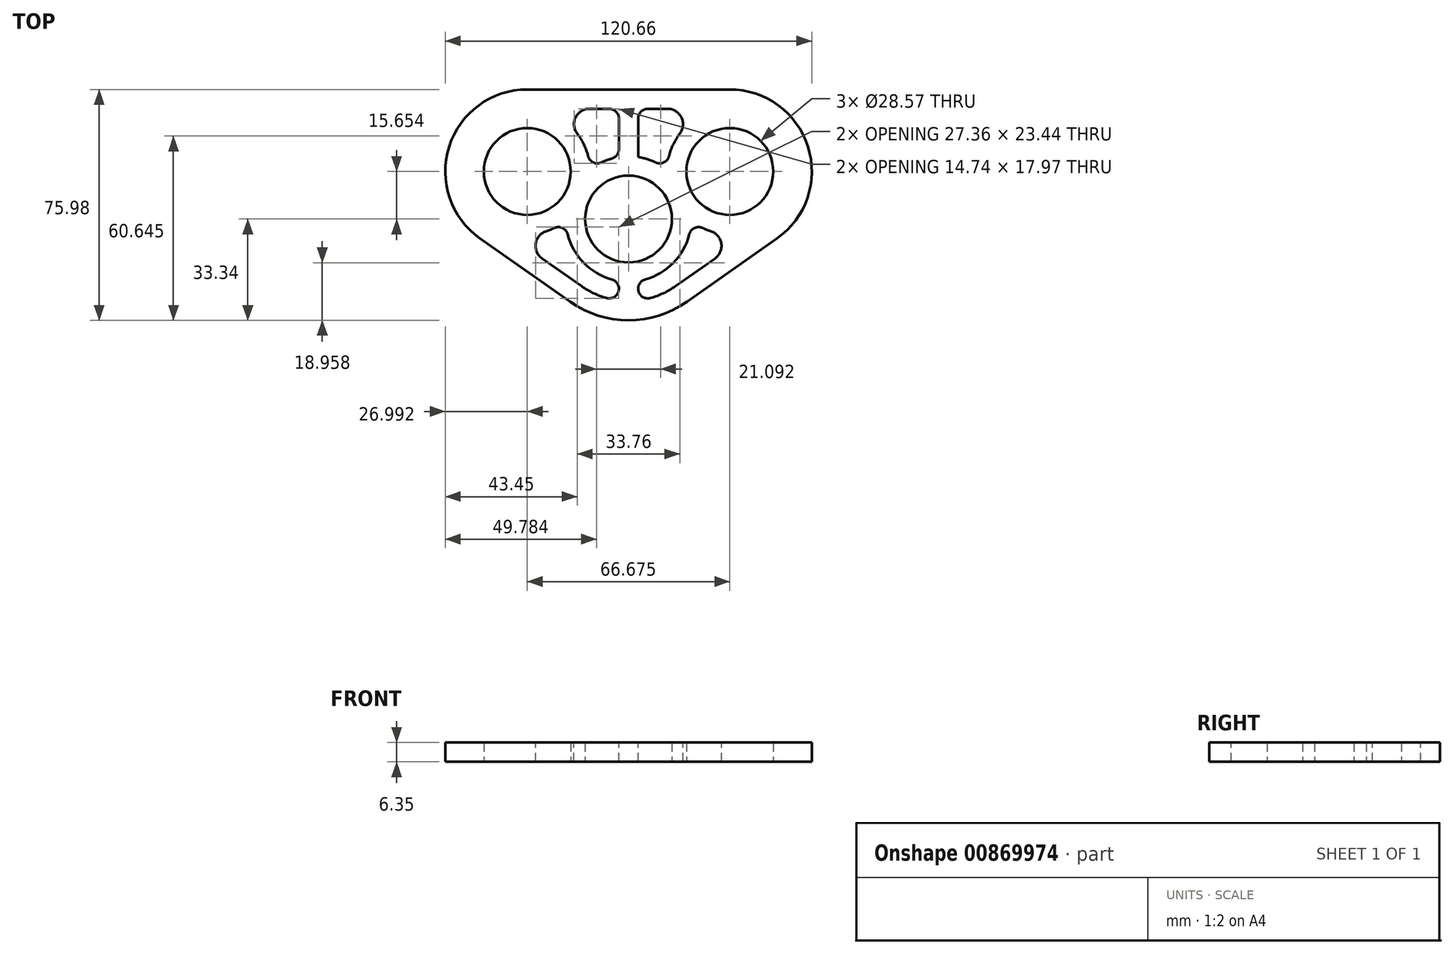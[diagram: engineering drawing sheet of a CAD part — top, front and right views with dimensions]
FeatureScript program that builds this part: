
annotation { "Feature Type Name" : "Feature", "Feature Type Description" : "" }
export const myFeature = defineFeature(function(context is Context, id is Id, definition is map)
    precondition{}
    {
        {
            var Q0;
            Q0=qCreatedBy(makeId("Top.planeOp"),FACE);
            var sketch = newSketch(context, id + "F0", { "sketchPlane" : qUnion([Q0])});
            skCircle(sketch, "E0", {"center": v(0, 0) * mm, "radius": 27.94 * mm, "construction": true});
            skCircle(sketch, "E1.0", {"center": v(0, 0) * mm, "radius": 30.48 * mm, "construction": true});
            skCircle(sketch, "E2", {"center": v(-33.34, 15.65) * mm, "radius": 8.9 * mm, "construction": true});
            skCircle(sketch, "E3.0", {"center": v(-33.34, 15.65) * mm, "radius": 11.43 * mm, "construction": true});
            skLineSegment(sketch, "E4", {"start": v(-33.34, 15.65) * mm, "end": v(0, 0) * mm, "construction": true});
            skLineSegment(sketch, "E5", {"start": v(0, 0) * mm, "end": v(0, -42.35) * mm, "construction": true});
            skLineSegment(sketch, "E6.MirrorCS", {"start": v(33.34, 15.65) * mm, "end": v(0, 0) * mm, "construction": true});
            skCircle(sketch, "E7.MirrorC", {"center": v(33.34, 15.65) * mm, "radius": 8.9 * mm, "construction": true});
            skCircle(sketch, "E8.MirrorC", {"center": v(33.34, 15.65) * mm, "radius": 11.43 * mm, "construction": true});
            skCircle(sketch, "E9", {"center": v(-33.34, 15.65) * mm, "radius": 31.75 * mm, "construction": true});
            skCircle(sketch, "E10", {"center": v(33.34, 15.65) * mm, "radius": 31.75 * mm, "construction": true});
            skLineSegment(sketch, "E11", {"start": v(-33.34, 15.65) * mm, "end": v(33.34, 15.65) * mm, "construction": true});
            skPoint(sketch, "E12", {"position": v(-1.59, 15.65) * mm});
            skPoint(sketch, "E12.positionSnap0", {"position": v(0, 15.65) * mm});
            skPoint(sketch, "E13", {"position": v(1.59, 15.65) * mm});
            skCircle(sketch, "E14", {"center": v(-33.34, 15.65) * mm, "radius": 14.29 * mm});
            skCircle(sketch, "E15", {"center": v(33.34, 15.65) * mm, "radius": 14.29 * mm});
            skCircle(sketch, "E16", {"center": v(0, 0) * mm, "radius": 14.29 * mm});
            skCircle(sketch, "E17.0", {"center": v(0, 0) * mm, "radius": 33.34 * mm});
            skCircle(sketch, "E18.0", {"center": v(-33.34, 15.65) * mm, "radius": 26.99 * mm});
            skCircle(sketch, "E19.0", {"center": v(33.34, 15.65) * mm, "radius": 26.99 * mm});
            skLineSegment(sketch, "E20", {"start": v(-33.34, 42.64) * mm, "end": v(33.34, 42.64) * mm});
            skLineSegment(sketch, "E21", {"start": v(-19.16, -27.28) * mm, "end": v(-48.85, -6.43) * mm});
            skLineSegment(sketch, "E22", {"start": v(19.16, -27.28) * mm, "end": v(48.85, -6.43) * mm});
            skSolve(sketch);
        }
        {
            var Q0;
            {var subQ2=sQuery(id+"F0.wireOp",EDGE,"E17.0");var subQ4=sQuery(id+"F0.wireOp",EDGE,"E14");var subQ7=makeQuery(id+"F0.imprint","INTERSECT",VERTEX,{"disambiguationData":[OD(0.0)],"derivedFrom":[subQ4,subQ2]});Q0=makeQuery(id+"F0.imprint","IMPRINT",FACE,{"disambiguationData":[TD([[makeQuery(id+"F0.imprint","IMPRINT",EDGE,{"disambiguationData":[TD([[subQ7,-1.0]])],"derivedFrom":subQ4}),-1.0]])]});}
            var Q1;
            {var subQ5=sQuery(id+"F0.wireOp",EDGE,"E20");Q1=makeQuery(id+"F0.imprint","IMPRINT",FACE,{"disambiguationData":[TD([[makeQuery(id+"F0.imprint","IMPRINT",EDGE,{"derivedFrom":subQ5}),-1.0]])]});}
            var Q2;
            {var subQ0=sQuery(id+"F0.wireOp",EDGE,"E17.0");var subQ1=sQuery(id+"F0.wireOp",EDGE,"E15");var subQ8=makeQuery(id+"F0.imprint","INTERSECT",VERTEX,{"disambiguationData":[OD(0.0)],"derivedFrom":[subQ1,subQ0]});Q2=makeQuery(id+"F0.imprint","IMPRINT",FACE,{"disambiguationData":[TD([[makeQuery(id+"F0.imprint","IMPRINT",EDGE,{"disambiguationData":[TD([[subQ8,1.0]])],"derivedFrom":subQ1}),-1.0]])]});}
            var Q3;
            {var subQ0=sQuery(id+"F0.wireOp",EDGE,"E17.0");var subQ1=sQuery(id+"F0.wireOp",EDGE,"E15");var subQ2=makeQuery(id+"F0.imprint","INTERSECT",VERTEX,{"disambiguationData":[OD(0.0)],"derivedFrom":[subQ1,subQ0]});Q3=makeQuery(id+"F0.imprint","IMPRINT",FACE,{"disambiguationData":[TD([[makeQuery(id+"F0.imprint","IMPRINT",EDGE,{"disambiguationData":[TD([[subQ2,-1.0]])],"derivedFrom":subQ1}),-1.0]])]});}
            var Q4;
            {var subQ0=sQuery(id+"F0.wireOp",EDGE,"E18.0");var subQ1=sQuery(id+"F0.wireOp",EDGE,"E16");var subQ2=makeQuery(id+"F0.imprint","INTERSECT",VERTEX,{"disambiguationData":[OD(0.0)],"derivedFrom":[subQ1,subQ0]});Q4=makeQuery(id+"F0.imprint","IMPRINT",FACE,{"disambiguationData":[TD([[makeQuery(id+"F0.imprint","IMPRINT",EDGE,{"disambiguationData":[TD([[subQ2,1.0]])],"derivedFrom":subQ1}),-1.0]])]});}
            var Q5;
            {var subQ0=sQuery(id+"F0.wireOp",EDGE,"E17.0");var subQ1=sQuery(id+"F0.wireOp",EDGE,"E14");var subQ8=makeQuery(id+"F0.imprint","INTERSECT",VERTEX,{"disambiguationData":[OD(0.0)],"derivedFrom":[subQ1,subQ0]});Q5=makeQuery(id+"F0.imprint","IMPRINT",FACE,{"disambiguationData":[TD([[makeQuery(id+"F0.imprint","IMPRINT",EDGE,{"disambiguationData":[TD([[subQ8,1.0]])],"derivedFrom":subQ1}),-1.0]])]});}
            var Q6;
            {var subQ3=sQuery(id+"F0.wireOp",EDGE,"E18.0");var subQ7=sQuery(id+"F0.wireOp",EDGE,"E16");var subQ9=makeQuery(id+"F0.imprint","INTERSECT",VERTEX,{"disambiguationData":[OD(1.0)],"derivedFrom":[subQ7,subQ3]});Q6=makeQuery(id+"F0.imprint","IMPRINT",FACE,{"disambiguationData":[TD([[makeQuery(id+"F0.imprint","IMPRINT",EDGE,{"disambiguationData":[TD([[subQ9,-1.0]])],"derivedFrom":subQ7}),-1.0]])]});}
            var Q7;
            {var subQ0=sQuery(id+"F0.wireOp",EDGE,"E21");Q7=makeQuery(id+"F0.imprint","IMPRINT",FACE,{"disambiguationData":[TD([[makeQuery(id+"F0.imprint","IMPRINT",EDGE,{"derivedFrom":subQ0}),-1.0]])]});}
            var Q8;
            {var subQ0=sQuery(id+"F0.wireOp",EDGE,"E22");Q8=makeQuery(id+"F0.imprint","IMPRINT",FACE,{"disambiguationData":[TD([[makeQuery(id+"F0.imprint","IMPRINT",EDGE,{"derivedFrom":subQ0}),1.0]])]});}
            extrude(context, id + "F1", {"entities" : qUnion([Q0, Q1, Q2, Q3, Q4, Q5, Q6, Q7, Q8]), "depth" : 6.35 * mm, "offsetDistance" : 25.4 * mm});
        }
        {
            var Q0;
            Q0=makeQuery(id+"F1.opExtrude","CAP_FACE",FACE,{"disambiguationData":[OSD([sQuery(id+"F0.wireOp",EDGE,"E14"),sQuery(id+"F0.wireOp",EDGE,"E15"),sQuery(id+"F0.wireOp",EDGE,"E16"),sQuery(id+"F0.wireOp",EDGE,"E17.0"),sQuery(id+"F0.wireOp",EDGE,"E18.0"),sQuery(id+"F0.wireOp",EDGE,"E19.0"),sQuery(id+"F0.wireOp",EDGE,"E20"),sQuery(id+"F0.wireOp",EDGE,"E21"),sQuery(id+"F0.wireOp",EDGE,"E22")])],"isStart":false});
            var sketch = newSketch(context, id + "F2", { "sketchPlane" : qUnion([Q0])});
            skLineSegment(sketch, "E23.0", {"start": v(33.34, 36.3) * mm, "end": v(-33.34, 36.3) * mm});
            skLineSegment(sketch, "E23.1", {"start": v(-45.2, -1.23) * mm, "end": v(-15.51, -22.08) * mm});
            skArc(sketch, "E23.2", {"start": v(-15.51, -22.08) * mm, "mid": v(0, -26.99) * mm, "end": v(15.51, -22.08) * mm});
            skArc(sketch, "E23.3", {"start": v(-33.34, 36.3) * mm, "mid": v(-53.02, 21.87) * mm, "end": v(-45.2, -1.23) * mm});
            skLineSegment(sketch, "E23.4", {"start": v(15.51, -22.08) * mm, "end": v(45.2, -1.23) * mm});
            skArc(sketch, "E23.5", {"start": v(45.2, -1.23) * mm, "mid": v(53.02, 21.87) * mm, "end": v(33.34, 36.3) * mm});
            skCircle(sketch, "E24.0", {"center": v(33.34, 15.65) * mm, "radius": 20.64 * mm});
            skCircle(sketch, "E25.0", {"center": v(0, 0) * mm, "radius": 20.64 * mm});
            skCircle(sketch, "E26.0", {"center": v(-33.34, 15.65) * mm, "radius": 20.64 * mm});
            skLineSegment(sketch, "E27", {"start": v(0, -26.99) * mm, "end": v(0, -20.64) * mm, "construction": true});
            skLineSegment(sketch, "E28", {"start": v(0, 20.64) * mm, "end": v(0, 36.3) * mm, "construction": true});
            skLineSegment(sketch, "E29.0", {"start": v(3.18, -26.8) * mm, "end": v(3.18, -20.4) * mm});
            skLineSegment(sketch, "E30.0", {"start": v(33.34, 49) * mm, "end": v(-33.34, 49) * mm});
            skLineSegment(sketch, "E30.1", {"start": v(-52.5, -11.63) * mm, "end": v(-22.81, -32.48) * mm});
            skArc(sketch, "E30.2", {"start": v(-22.81, -32.48) * mm, "mid": v(0, -39.69) * mm, "end": v(22.81, -32.48) * mm});
            skArc(sketch, "E30.3", {"start": v(-33.34, 49) * mm, "mid": v(-65.12, 25.7) * mm, "end": v(-52.5, -11.63) * mm});
            skLineSegment(sketch, "E30.4", {"start": v(22.81, -32.48) * mm, "end": v(52.5, -11.63) * mm});
            skArc(sketch, "E30.5", {"start": v(52.5, -11.63) * mm, "mid": v(65.12, 25.7) * mm, "end": v(33.34, 49) * mm});
            skLineSegment(sketch, "E31.0", {"start": v(-3.17, -26.8) * mm, "end": v(-3.17, -20.4) * mm});
            skLineSegment(sketch, "E32.0", {"start": v(3.18, 20.4) * mm, "end": v(3.17, 36.3) * mm});
            skLineSegment(sketch, "E33.0", {"start": v(-3.18, 20.4) * mm, "end": v(-3.18, 36.3) * mm});
            skSolve(sketch);
        }
        {
            var Q0;
            {var subQ3=sQuery(id+"F2.wireOp",EDGE,"E33.0");Q0=makeQuery(id+"F2.imprint","IMPRINT",FACE,{"disambiguationData":[TD([[makeQuery(id+"F2.imprint","IMPRINT",EDGE,{"derivedFrom":subQ3}),1.0]])]});}
            var Q1;
            {var subQ3=sQuery(id+"F2.wireOp",EDGE,"E32.0");Q1=makeQuery(id+"F2.imprint","IMPRINT",FACE,{"disambiguationData":[TD([[makeQuery(id+"F2.imprint","IMPRINT",EDGE,{"derivedFrom":subQ3}),-1.0]])]});}
            var Q2;
            {var subQ1=sQuery(id+"F2.wireOp",EDGE,"E23.1");Q2=makeQuery(id+"F2.imprint","IMPRINT",FACE,{"disambiguationData":[TD([[makeQuery(id+"F2.imprint","IMPRINT",EDGE,{"derivedFrom":subQ1}),1.0]])]});}
            var Q3;
            {var subQ4=sQuery(id+"F2.wireOp",EDGE,"E23.4");Q3=makeQuery(id+"F2.imprint","IMPRINT",FACE,{"disambiguationData":[TD([[makeQuery(id+"F2.imprint","IMPRINT",EDGE,{"derivedFrom":subQ4}),1.0]])]});}
            extrude(context, id + "F3", {"entities" : qUnion([Q0, Q1, Q2, Q3]), "operationType" : NewBodyOperationType.REMOVE, "depth" : -6.35 * mm, "offsetDistance" : 25.4 * mm});
        }
        {
            var Q0;
            Q0=makeQuery(id+"F3.boolean.opBoolean","COPY",EDGE,{"derivedFrom":makeQuery(id+"F3.opExtrude","SWEPT_EDGE",EDGE,{"disambiguationData":[OSD([sQuery(id+"F2.wireOp",EDGE,"E25.0"),sQuery(id+"F2.wireOp",EDGE,"E29.0")])]})});
            var Q1;
            Q1=makeQuery(id+"F3.boolean.opBoolean","COPY",EDGE,{"derivedFrom":makeQuery(id+"F3.opExtrude","SWEPT_EDGE",EDGE,{"disambiguationData":[OSD([sQuery(id+"F2.wireOp",EDGE,"E23.0"),sQuery(id+"F2.wireOp",EDGE,"E32.0")])]})});
            var Q2;
            {var subQ0=sQuery(id+"F2.wireOp",EDGE,"E25.0");var subQ1=sQuery(id+"F2.wireOp",EDGE,"E24.0");Q2=makeQuery(id+"F3.boolean.opBoolean","COPY",EDGE,{"derivedFrom":makeQuery(id+"F3.opExtrude","SWEPT_EDGE",EDGE,{"disambiguationData":[OSD([subQ1,subQ0]),TDD([makeQuery(id+"F2.imprint","INTERSECT",VERTEX,{"disambiguationData":[OD(1.0)],"derivedFrom":[subQ1,subQ0]})])]})});}
            var Q3;
            Q3=makeQuery(id+"F3.boolean.opBoolean","COPY",EDGE,{"derivedFrom":makeQuery(id+"F3.opExtrude","SWEPT_EDGE",EDGE,{"disambiguationData":[OSD([sQuery(id+"F2.wireOp",EDGE,"E23.2"),sQuery(id+"F2.wireOp",EDGE,"E29.0")])]})});
            var Q4;
            Q4=makeQuery(id+"F3.boolean.opBoolean","COPY",EDGE,{"derivedFrom":makeQuery(id+"F3.opExtrude","SWEPT_EDGE",EDGE,{"disambiguationData":[OSD([sQuery(id+"F2.wireOp",EDGE,"E23.2"),sQuery(id+"F2.wireOp",EDGE,"E31.0")])]})});
            var Q5;
            Q5=makeQuery(id+"F3.boolean.opBoolean","COPY",EDGE,{"derivedFrom":makeQuery(id+"F3.opExtrude","SWEPT_EDGE",EDGE,{"disambiguationData":[OSD([sQuery(id+"F2.wireOp",EDGE,"E25.0"),sQuery(id+"F2.wireOp",EDGE,"E31.0")])]})});
            var Q6;
            {var subQ0=sQuery(id+"F2.wireOp",EDGE,"E26.0");var subQ1=sQuery(id+"F2.wireOp",EDGE,"E25.0");Q6=makeQuery(id+"F3.boolean.opBoolean","COPY",EDGE,{"derivedFrom":makeQuery(id+"F3.opExtrude","SWEPT_EDGE",EDGE,{"disambiguationData":[OSD([subQ1,subQ0]),TDD([makeQuery(id+"F2.imprint","INTERSECT",VERTEX,{"disambiguationData":[OD(1.0)],"derivedFrom":[subQ1,subQ0]})])]})});}
            var Q7;
            Q7=makeQuery(id+"F3.boolean.opBoolean","COPY",EDGE,{"derivedFrom":makeQuery(id+"F3.opExtrude","SWEPT_EDGE",EDGE,{"disambiguationData":[OSD([sQuery(id+"F2.wireOp",EDGE,"E23.0"),sQuery(id+"F2.wireOp",EDGE,"E33.0")])]})});
            var Q8;
            Q8=makeQuery(id+"F3.boolean.opBoolean","COPY",EDGE,{"derivedFrom":makeQuery(id+"F3.opExtrude","SWEPT_EDGE",EDGE,{"disambiguationData":[OSD([sQuery(id+"F2.wireOp",EDGE,"E25.0"),sQuery(id+"F2.wireOp",EDGE,"E33.0")])]})});
            var Q9;
            {var subQ0=sQuery(id+"F2.wireOp",EDGE,"E26.0");var subQ1=sQuery(id+"F2.wireOp",EDGE,"E25.0");Q9=makeQuery(id+"F3.boolean.opBoolean","COPY",EDGE,{"derivedFrom":makeQuery(id+"F3.opExtrude","SWEPT_EDGE",EDGE,{"disambiguationData":[OSD([subQ1,subQ0]),TDD([makeQuery(id+"F2.imprint","INTERSECT",VERTEX,{"disambiguationData":[OD(0.0)],"derivedFrom":[subQ1,subQ0]})])]})});}
            var Q10;
            {var subQ0=sQuery(id+"F2.wireOp",EDGE,"E25.0");var subQ1=sQuery(id+"F2.wireOp",EDGE,"E24.0");Q10=makeQuery(id+"F3.boolean.opBoolean","COPY",EDGE,{"derivedFrom":makeQuery(id+"F3.opExtrude","SWEPT_EDGE",EDGE,{"disambiguationData":[OSD([subQ1,subQ0]),TDD([makeQuery(id+"F2.imprint","INTERSECT",VERTEX,{"disambiguationData":[OD(0.0)],"derivedFrom":[subQ1,subQ0]})])]})});}
            fillet(context, id + "F4", {"entities" : qUnion([Q0, Q1, Q2, Q3, Q4, Q5, Q6, Q7, Q8, Q9, Q10]), "radius" : 3.17 * mm, "tangentPropagation" : true, "allowEdgeOverflow" : false});
        }
        {
            var Q0;
            Q0=makeQuery(id+"F3.boolean.opBoolean","COPY",EDGE,{"derivedFrom":makeQuery(id+"F3.opExtrude","SWEPT_EDGE",EDGE,{"disambiguationData":[OSD([sQuery(id+"F2.wireOp",EDGE,"E23.4"),sQuery(id+"F2.wireOp",EDGE,"E24.0")])]})});
            var Q1;
            Q1=makeQuery(id+"F3.boolean.opBoolean","COPY",EDGE,{"derivedFrom":makeQuery(id+"F3.opExtrude","SWEPT_EDGE",EDGE,{"disambiguationData":[OSD([sQuery(id+"F2.wireOp",EDGE,"E23.0"),sQuery(id+"F2.wireOp",EDGE,"E24.0")])]})});
            var Q2;
            Q2=makeQuery(id+"F3.boolean.opBoolean","COPY",EDGE,{"derivedFrom":makeQuery(id+"F3.opExtrude","SWEPT_EDGE",EDGE,{"disambiguationData":[OSD([sQuery(id+"F2.wireOp",EDGE,"E23.0"),sQuery(id+"F2.wireOp",EDGE,"E26.0")])]})});
            var Q3;
            Q3=makeQuery(id+"F3.boolean.opBoolean","COPY",EDGE,{"derivedFrom":makeQuery(id+"F3.opExtrude","SWEPT_EDGE",EDGE,{"disambiguationData":[OSD([sQuery(id+"F2.wireOp",EDGE,"E23.1"),sQuery(id+"F2.wireOp",EDGE,"E26.0")])]})});
            fillet(context, id + "F5", {"entities" : qUnion([Q0, Q1, Q2, Q3]), "radius" : 5.08 * mm, "tangentPropagation" : true, "allowEdgeOverflow" : false});
        }
    });
